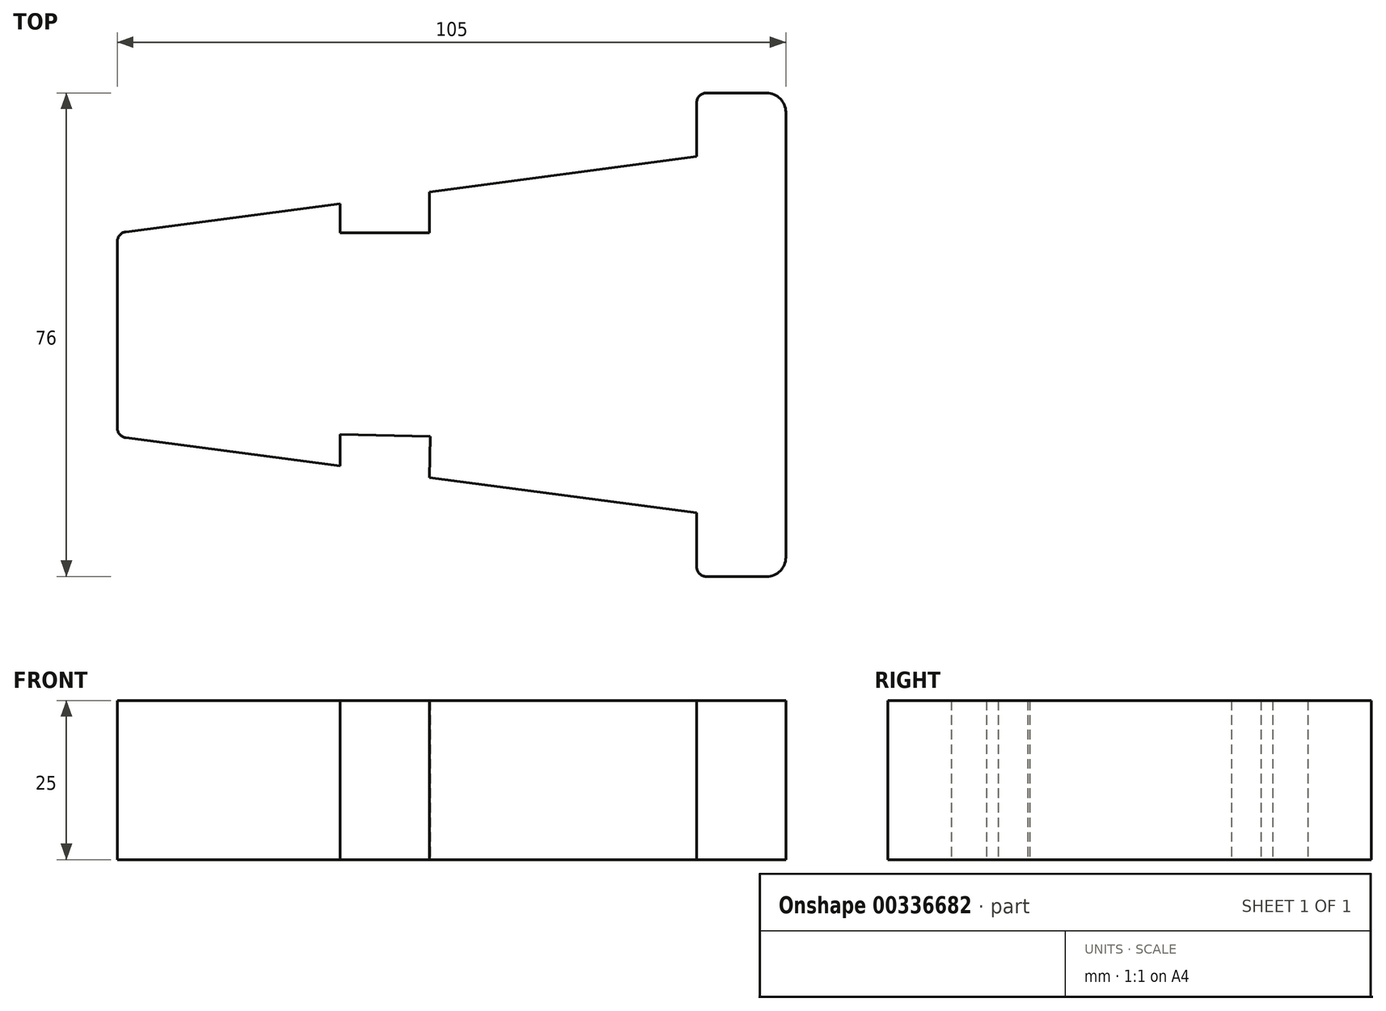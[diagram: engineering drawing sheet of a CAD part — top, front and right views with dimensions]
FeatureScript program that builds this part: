
annotation { "Feature Type Name" : "Feature", "Feature Type Description" : "" }
export const myFeature = defineFeature(function(context is Context, id is Id, definition is map)
    precondition{}
    {
        {
            var Q0;
            Q0=qCreatedBy(makeId("Top.planeOp"),FACE);
            var sketch = newSketch(context, id + "F0", { "sketchPlane" : qUnion([Q0])});
            skLineSegment(sketch, "E0", {"start": v(55.9, 46.9) * mm, "end": v(55.9, -23.1) * mm});
            skLineSegment(sketch, "E1", {"start": v(52.9, 49.9) * mm, "end": v(43.4, 49.9) * mm});
            skLineSegment(sketch, "E2", {"start": v(52.9, -26.1) * mm, "end": v(43.4, -26.1) * mm});
            skLineSegment(sketch, "E3", {"start": v(41.9, 48.4) * mm, "end": v(41.9, 39.9) * mm});
            skLineSegment(sketch, "E4", {"start": v(41.9, -24.6) * mm, "end": v(41.9, -16.1) * mm});
            skPoint(sketch, "E5.visualSharp", {"position": v(55.9, 49.9) * mm});
            skArc(sketch, "E5.filletArc", {"start": v(55.9, 46.9) * mm, "mid": v(55.01, 49.02) * mm, "end": v(52.9, 49.9) * mm});
            skPoint(sketch, "E6.visualSharp", {"position": v(55.9, -26.1) * mm});
            skArc(sketch, "E6.filletArc", {"start": v(52.9, -26.1) * mm, "mid": v(55.01, -25.22) * mm, "end": v(55.9, -23.1) * mm});
            skPoint(sketch, "E7.visualSharp", {"position": v(41.9, 49.9) * mm});
            skArc(sketch, "E7.filletArc", {"start": v(43.4, 49.9) * mm, "mid": v(42.33, 49.46) * mm, "end": v(41.9, 48.4) * mm});
            skPoint(sketch, "E8.visualSharp", {"position": v(41.9, -26.1) * mm});
            skArc(sketch, "E8.filletArc", {"start": v(41.9, -24.6) * mm, "mid": v(42.33, -25.66) * mm, "end": v(43.4, -26.1) * mm});
            skPoint(sketch, "E9.end.orphan", {"position": v(0, -13.1) * mm});
            skPoint(sketch, "E10.end.orphan", {"position": v(0, 36.9) * mm});
            skPoint(sketch, "E11.endSnap0", {"position": v(55.9, 11.9) * mm});
            skLineSegment(sketch, "E12", {"start": v(-49.1, 11.9) * mm, "end": v(-49.1, -2.78) * mm});
            skLineSegment(sketch, "E13", {"start": v(-49.1, 11.9) * mm, "end": v(-49.1, 26.59) * mm});
            skLineSegment(sketch, "E14", {"start": v(-47.8, 28.07) * mm, "end": v(-14.1, 32.52) * mm});
            skLineSegment(sketch, "E15", {"start": v(-47.8, -4.27) * mm, "end": v(-14.1, -8.71) * mm});
            skLineSegment(sketch, "E16.trimOffspring", {"start": v(-0.1, 34.36) * mm, "end": v(41.9, 39.9) * mm});
            skLineSegment(sketch, "E17.trimOffspring", {"start": v(-0.1, -10.56) * mm, "end": v(41.9, -16.1) * mm});
            skPoint(sketch, "E11.start.orphan", {"position": v(55.9, 11.9) * mm});
            skPoint(sketch, "E18.end.orphan", {"position": v(0, -5) * mm});
            skPoint(sketch, "E19.orphan", {"position": v(0, 5) * mm});
            skLineSegment(sketch, "E20.trimOffspring", {"start": v(-0.1, 11.9) * mm, "end": v(-0.03, 11.9) * mm});
            skLineSegment(sketch, "E21", {"start": v(-0.1, 27.9) * mm, "end": v(-0.1, 34.36) * mm});
            skLineSegment(sketch, "E22", {"start": v(0.04, -4.1) * mm, "end": v(-0.1, -10.56) * mm});
            skLineSegment(sketch, "E23", {"start": v(-14.1, 27.9) * mm, "end": v(-0.1, 27.9) * mm});
            skLineSegment(sketch, "E24", {"start": v(-14.1, 27.9) * mm, "end": v(-14.1, 32.52) * mm});
            skLineSegment(sketch, "E25", {"start": v(0.04, -4.1) * mm, "end": v(-14.1, -3.77) * mm});
            skLineSegment(sketch, "E26", {"start": v(-14.1, -3.77) * mm, "end": v(-14.1, -8.71) * mm});
            skPoint(sketch, "E27.end.orphan", {"position": v(0, -23.37) * mm});
            skPoint(sketch, "E28.trimOffspring.end.orphan", {"position": v(-0.1, 55.79) * mm});
            skPoint(sketch, "E29.start.orphan", {"position": v(-49.1, 55.79) * mm});
            skPoint(sketch, "E30.start.orphan", {"position": v(-14.1, 55.79) * mm});
            skPoint(sketch, "E31.visualSharp", {"position": v(-49.1, 27.9) * mm});
            skArc(sketch, "E31.filletArc", {"start": v(-47.8, 28.07) * mm, "mid": v(-48.73, 27.58) * mm, "end": v(-49.1, 26.59) * mm});
            skPoint(sketch, "E32.visualSharp", {"position": v(-49.1, -4.1) * mm});
            skArc(sketch, "E32.filletArc", {"start": v(-49.1, -2.78) * mm, "mid": v(-48.73, -3.77) * mm, "end": v(-47.8, -4.27) * mm});
            skSolve(sketch);
        }
        {
            var Q0;
            Q0=makeQuery(id+"F0.imprint","IMPRINT",FACE,{"disambiguationData":[TD([[makeQuery(id+"F0.imprint","IMPRINT",EDGE,{"derivedFrom":sQuery(id+"F0.wireOp",EDGE,"E0")}),-1.0]])]});
            extrude(context, id + "F1", {"entities" : qUnion([Q0]), "depth" : 25 * mm});
        }
    });
